# Revit family: PRD_AR_SpDspnsrs_STRATOSSoapDispenser_STR619N_STR619EN
name_source: partatom
category: Specialty Equipment
units: mm (PartAtom-declared; Revit-internal decimal feet)

## family parameters
Cut with Voids When Loaded = No
Host = Face
OmniClass Number = 23.40.20.21.34
OmniClass Title = Soap Holders, Dispensers
Part Type = Normal
Room Calculation Point = No
Round Connector Dimension = Use Diameter
Shared = No

## types (2) — shared parameters
AssetType = Fixed
Category = Pr_40_70_22_81, Soap dispensers
Default Elevation = 850 mm  [stored 2.78871 ft]
DurationUnit = year
Features = stainless steel, satin finished
FillingQuantity = 1
FillingQuantityUom = Liter
Finish = Satin finished
IfcExportAs = IfcFurnitureType
IfcExportType = USERDEFINED
IntegralAccessories = incl. stainless steel screws and dowels
IsBuiltIn = TRUE
Lock = Key-lock
MainColor = Stainless steel
Manufacturer = KWC Group Management AG
ManufacturerName = KWC Group Management AG
ManufacturerURL = www.kwc-professional.com
Material = Stainless steel
MaterialCode = 1.4301
MaterialThickness = 1.50 mm
NBSDescription = Soap dispensers
NBSReference = 45-35-72/358
ProductInformation = http://pim.kwc.com
SoapDispenserMaterial = PRD_AR_StainlessSteel_SatinFinished
Style = Soap dispenser
TypeOfConsumable = Liquid soap
TypeOfFixing = Screw
TypeOfOperation = Manual operation
TypeOfSoapContainer = Integrated refillable tank
URL = www.kwc-professional.com
Uniclass2015Code = Pr_40_70_22_81
Uniclass2015Title = Soap dispenser
Uniclass2015Version = Products v1.10
Version = 1
WarrantyDurationUnit = year

## per-type parameters (varying)
| type | BIMObjectName | Description | GrossWeight | ModelNumber | ModelOffset | Name | NetWeight | NominalDepth | NominalHeight | NominalWidth | STR619EN | STR619N | Size | TypeOfMounting |
| STR619N | PRD_AR_SoapDispensers_STRATOSSoapDispenser_STR619N | STRATOS soap dispenser for wall mounting, stainless steel, surface satin finished, material thickness 1.5 mm, curved front with inspection window and push button for front operation, cylinder lock with key, suitable for liquid soap or lotion, 1000 ml refill container, including mounting material. | 1.76 kg | 3600008892 | 0 mm  [stored 0 ft] | STRATOS Soap dispenser STR619N | 1.56 kg | 150 mm | 154 mm  [stored 0.505249 ft] | 186 mm  [stored 0.610236 ft] | No | Yes | 186 x 154 x 150 mm | Wall mounting |
| STR619EN | PRD_AR_SoapDispensers_STRATOSSoapDispenser_STR619EN | STRATOS soap dispenser for recessed mounting, stainless steel, surface satin finished, material thickness 1.5 mm, curved front with inspection window and push button for front operation, cylinder lock with key, suitable for liquid soap or lotion, 1000 ml refill container, including mounting material. | 2.60 kg | 3600008890 | 57 mm  [stored 0.187008 ft] | STRATOS Soap dispenser STR619EN | 2.10 kg | 159 mm  [stored 0.521654 ft] | 181 mm  [stored 0.593832 ft] | 211 mm  [stored 0.692257 ft] | Yes | No | 211 x 181 x 159 mm | Recessed mounting |

note: column(s) folded — value = type name in every type: Model, ModelReference

note: [stored X ft] marks values corroborated as IEEE doubles in the binary element streams (Revit-internal decimal feet)

## geometry (parser evidence)
native form markers: Sweep x5
no freeform markers — native parametric forms only
